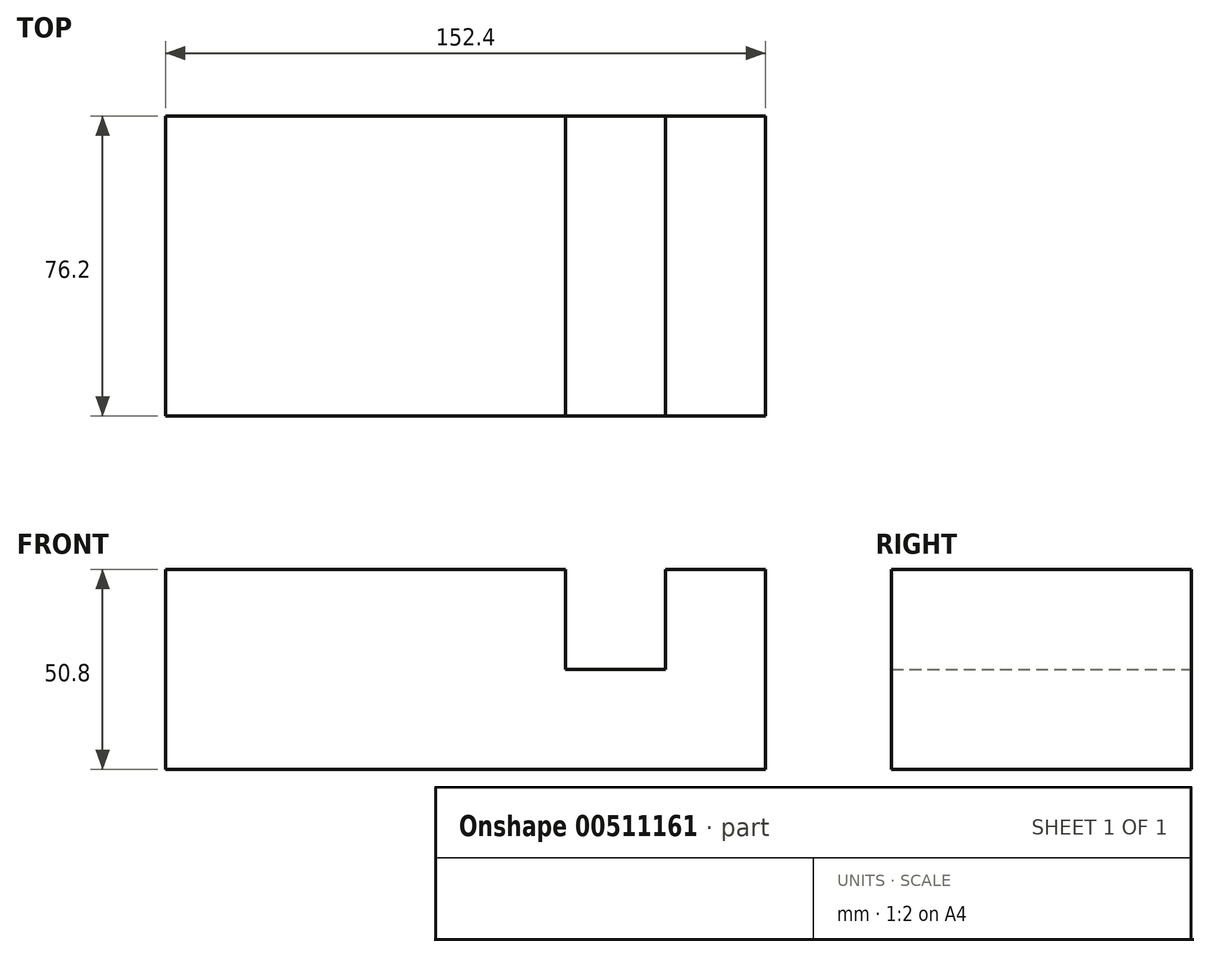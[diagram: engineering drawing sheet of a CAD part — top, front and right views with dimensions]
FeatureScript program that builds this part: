
annotation { "Feature Type Name" : "Feature", "Feature Type Description" : "" }
export const myFeature = defineFeature(function(context is Context, id is Id, definition is map)
    precondition{}
    {
        {
            var Q0;
            Q0=qCreatedBy(makeId("Front.planeOp"),FACE);
            var sketch = newSketch(context, id + "F0", { "sketchPlane" : qUnion([Q0])});
            skLineSegment(sketch, "E0", {"start": v(-78.63, -37.15) * mm, "end": v(73.77, -37.15) * mm});
            skLineSegment(sketch, "E1", {"start": v(73.77, -37.15) * mm, "end": v(73.77, 13.65) * mm});
            skLineSegment(sketch, "E2", {"start": v(73.77, 13.65) * mm, "end": v(48.37, 13.65) * mm});
            skLineSegment(sketch, "E3", {"start": v(48.37, 13.65) * mm, "end": v(48.37, -11.75) * mm});
            skLineSegment(sketch, "E4", {"start": v(48.37, -11.75) * mm, "end": v(22.97, -11.75) * mm});
            skLineSegment(sketch, "E5", {"start": v(22.97, -11.75) * mm, "end": v(22.97, 13.65) * mm});
            skLineSegment(sketch, "E6", {"start": v(22.97, 13.65) * mm, "end": v(-78.63, 13.65) * mm});
            skLineSegment(sketch, "E7", {"start": v(-78.63, 13.65) * mm, "end": v(-78.63, -37.15) * mm});
            skSolve(sketch);
        }
        {
            var Q0;
            Q0 = qSketchRegion(id + "F0", true);
            extrude(context, id + "F1", {"entities" : qUnion([Q0]), "depth" : 76.2 * mm});
        }
    });
